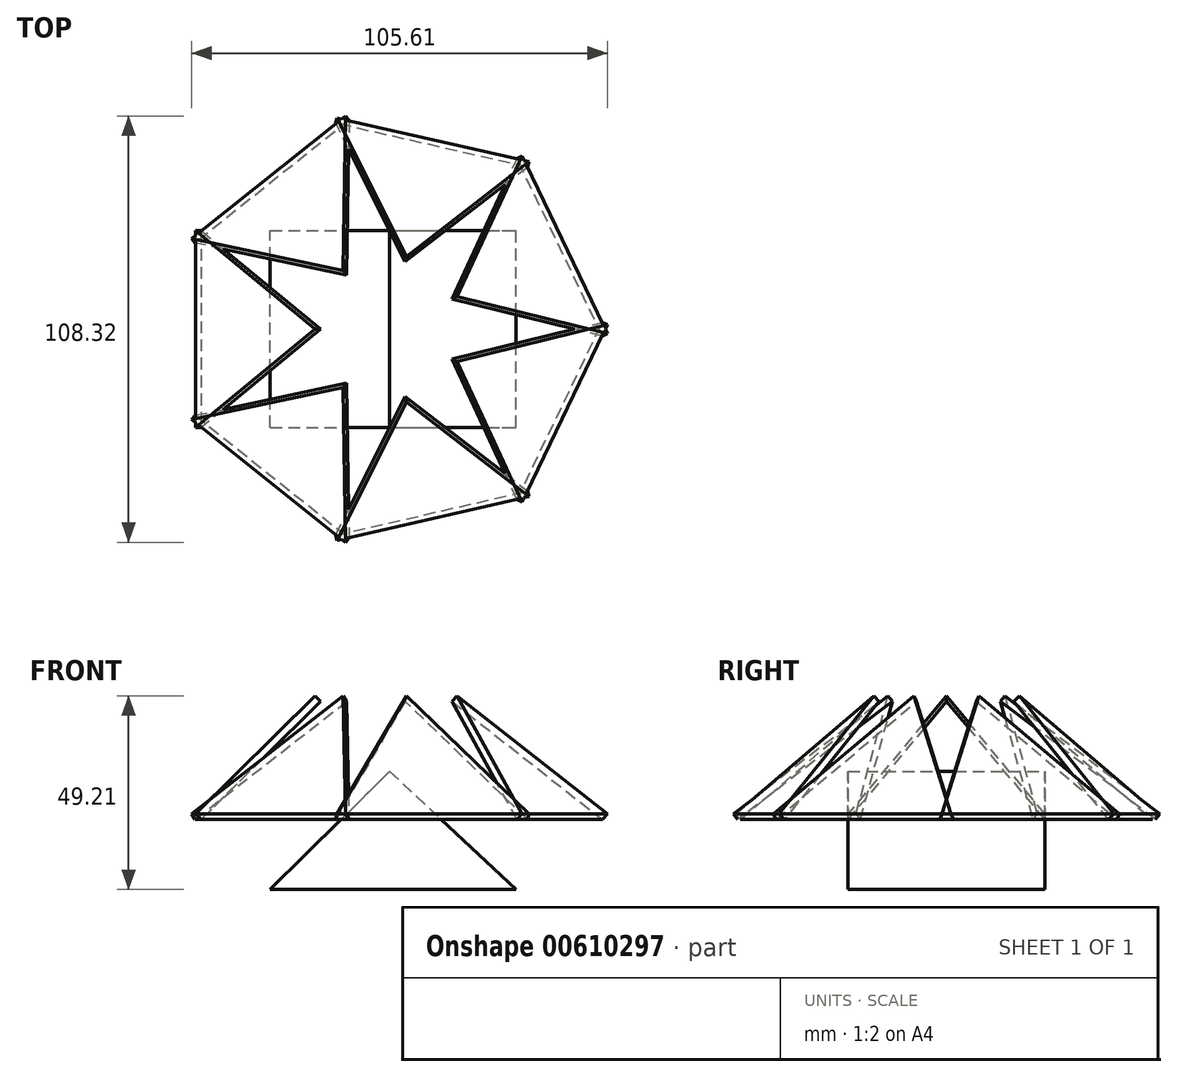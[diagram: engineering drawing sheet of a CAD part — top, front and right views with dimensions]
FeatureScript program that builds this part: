
annotation { "Feature Type Name" : "Feature", "Feature Type Description" : "" }
export const myFeature = defineFeature(function(context is Context, id is Id, definition is map)
    precondition{}
    {
        {
            var Q0;
            Q0=qCreatedBy(makeId("Front.planeOp"),FACE);
            var sketch = newSketch(context, id + "F0", { "sketchPlane" : qUnion([Q0])});
            skLineSegment(sketch, "E0.bottom", {"start": v(-30.37, 15) * mm, "end": v(32.13, 15) * mm, "construction": true});
            skLineSegment(sketch, "E0.top", {"start": v(-30.37, -15) * mm, "end": v(32.13, -15) * mm, "construction": true});
            skLineSegment(sketch, "E0.left", {"start": v(-30.37, 15) * mm, "end": v(-30.37, -15) * mm, "construction": true});
            skLineSegment(sketch, "E0.right", {"start": v(32.13, 15) * mm, "end": v(32.13, -15) * mm, "construction": true});
            skLineSegment(sketch, "E1", {"start": v(0, 0) * mm, "end": v(0, 15) * mm, "construction": true});
            skLineSegment(sketch, "E2", {"start": v(0, 0) * mm, "end": v(-30.37, 0) * mm, "construction": true});
            skLineSegment(sketch, "E3", {"start": v(-30.37, -15) * mm, "end": v(0, 15) * mm});
            skLineSegment(sketch, "E4", {"start": v(0, 15) * mm, "end": v(32.13, -15) * mm});
            skLineSegment(sketch, "E5", {"start": v(-30.37, -15) * mm, "end": v(32.13, -15) * mm});
            skLineSegment(sketch, "E6", {"start": v(0, 0) * mm, "end": v(0, 55.07) * mm});
            skPoint(sketch, "E6.endSnap0", {"position": v(0, 7.5) * mm});
            skSolve(sketch);
        }
        {
            var Q0;
            Q0=makeQuery(id+"F0.imprint","IMPRINT",FACE,{"disambiguationData":[TD([[makeQuery(id+"F0.imprint","IMPRINT",EDGE,{"derivedFrom":sQuery(id+"F0.wireOp",EDGE,"E3")}),-1.0]])]});
            extrude(context, id + "F1", {"entities" : qUnion([Q0]), "endBound" : BoundingType.SYMMETRIC, "depth" : 50 * mm, "offsetDistance" : 25 * mm});
        }
        {
            var Q0;
            Q0=makeQuery(id+"F1.opExtrude","SWEPT_FACE",FACE,{"disambiguationData":[OSD([sQuery(id+"F0.wireOp",EDGE,"E3")])]});
            cPlane(context, id + "F2", {"entities" : qUnion([Q0]), "cplaneType" : CPlaneType.OFFSET, "offset" : 25 * mm, "width" : 150 * mm, "height" : 150 * mm});
        }
        {
            var Q0;
            Q0=qCreatedBy(id+"F2.planeOp",FACE);
            var sketch = newSketch(context, id + "F3", { "sketchPlane" : qUnion([Q0])});
            skLineSegment(sketch, "E7.0.0", {"start": v(10.54, 25) * mm, "end": v(-32.14, 25) * mm});
            skLineSegment(sketch, "E7.0.1", {"start": v(-32.14, 25) * mm, "end": v(-32.14, -25) * mm});
            skLineSegment(sketch, "E7.0.2", {"start": v(-32.14, -25) * mm, "end": v(10.54, -25) * mm});
            skLineSegment(sketch, "E7.0.3", {"start": v(10.54, -25) * mm, "end": v(10.54, 25) * mm});
            skLineSegment(sketch, "E8", {"start": v(-32.14, 25) * mm, "end": v(10.54, 0) * mm});
            skLineSegment(sketch, "E9", {"start": v(10.54, 0) * mm, "end": v(-32.14, -25) * mm});
            skSolve(sketch);
        }
        {
            var Q0;
            Q0=makeQuery(id+"F3.imprint","IMPRINT",FACE,{"disambiguationData":[TD([[makeQuery(id+"F3.imprint","IMPRINT",EDGE,{"derivedFrom":sQuery(id+"F3.wireOp",EDGE,"E7.0.1")}),1.0]])]});
            extrude(context, id + "F4", {"entities" : qUnion([Q0]), "depth" : 2 * mm, "offsetDistance" : 25 * mm});
        }
        {
            var Q0;
            Q0=makeQuery(id+"F4.opExtrude","SWEPT_BODY",BODY,{"disambiguationData":[OSD([sQuery(id+"F3.wireOp",EDGE,"E7.0.0"),sQuery(id+"F3.wireOp",EDGE,"E7.0.1"),sQuery(id+"F3.wireOp",EDGE,"E7.0.2"),sQuery(id+"F3.wireOp",EDGE,"E7.0.3")])]});
            var Q1;
            Q1=sQuery(id+"F0.wireOp",EDGE,"E6");
            circularPattern(context, id + "F5", {"entities" : qUnion([Q0]), "axis" : qUnion([Q1]), "angle" : 360 * degree, "instanceCount" : 7, "equalSpace" : true});
        }
    });
